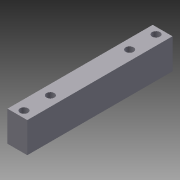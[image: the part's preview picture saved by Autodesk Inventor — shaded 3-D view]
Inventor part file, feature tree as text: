
AUTODESK INVENTOR PART (.ipt)
format: ipt  version: 2015 (Build 190159000, 159)  size: 115,200 bytes
history: native  units: mm
features: extrude x2, hole x2, chamfer x2, projected_geometry x1
ambient origin geometry x8: Origin, YZ Plane, XZ Plane, XY Plane, X Axis, Y Axis, Z Axis, Center Point
bodies: Solid1 (feature_tree)
feature tree (7):
  extrude  "Extrusión1"  Depth=15.0mm
  hole  "Agujero1"  [1 undecoded]
  extrude  "Extrusión2"  Depth=23.0mm TaperAngle=0.0deg
  chamfer  "Chaflán1"  Distance=100.0mm
  chamfer  "Chaflán2"  Distance=20.0mm
  hole  "Agujero2"  [1 undecoded]
  projected_geometry  "Contorno proyectado1"
note: 2 required parameter values undecoded (feature->parameter linkage not recoverable at this tier; creation-order binding heuristic only, values carry confidence <= 0.55)
